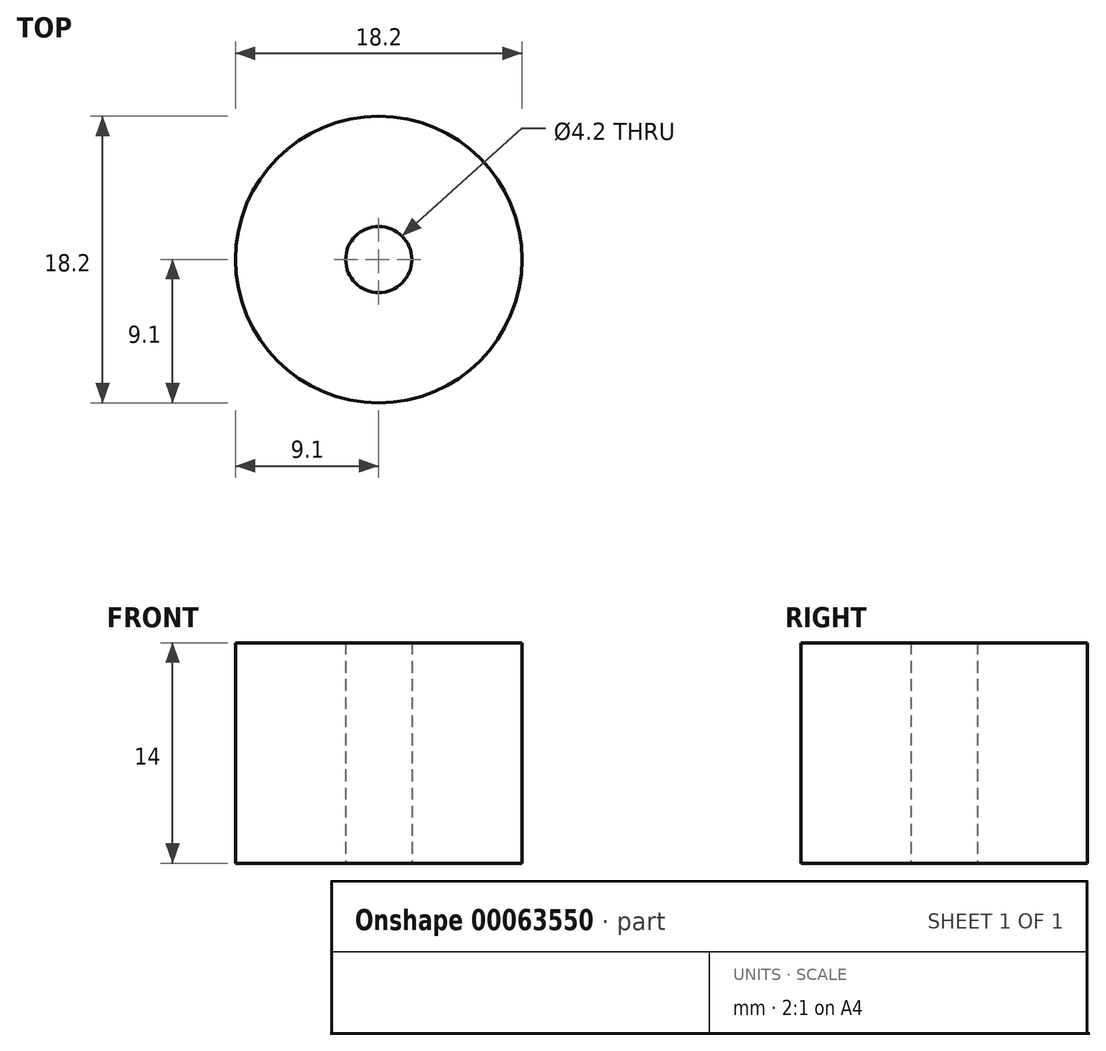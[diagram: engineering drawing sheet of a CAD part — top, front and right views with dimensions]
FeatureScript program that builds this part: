
annotation { "Feature Type Name" : "Feature", "Feature Type Description" : "" }
export const myFeature = defineFeature(function(context is Context, id is Id, definition is map)
    precondition{}
    {
        {
            var Q0;
            Q0=qCreatedBy(makeId("Top.planeOp"),FACE);
            var sketch = newSketch(context, id + "F0", { "sketchPlane" : qUnion([Q0])});
            skCircle(sketch, "E0", {"center": v(0, 0) * mm, "radius": 2.1 * mm});
            skCircle(sketch, "E1", {"center": v(0, 0) * mm, "radius": 9.1 * mm});
            skSolve(sketch);
        }
        {
            var Q0;
            Q0 = qSketchRegion(id + "F0", true);
            extrude(context, id + "F1", {"entities" : qUnion([Q0]), "depth" : 14 * mm});
        }
    });
